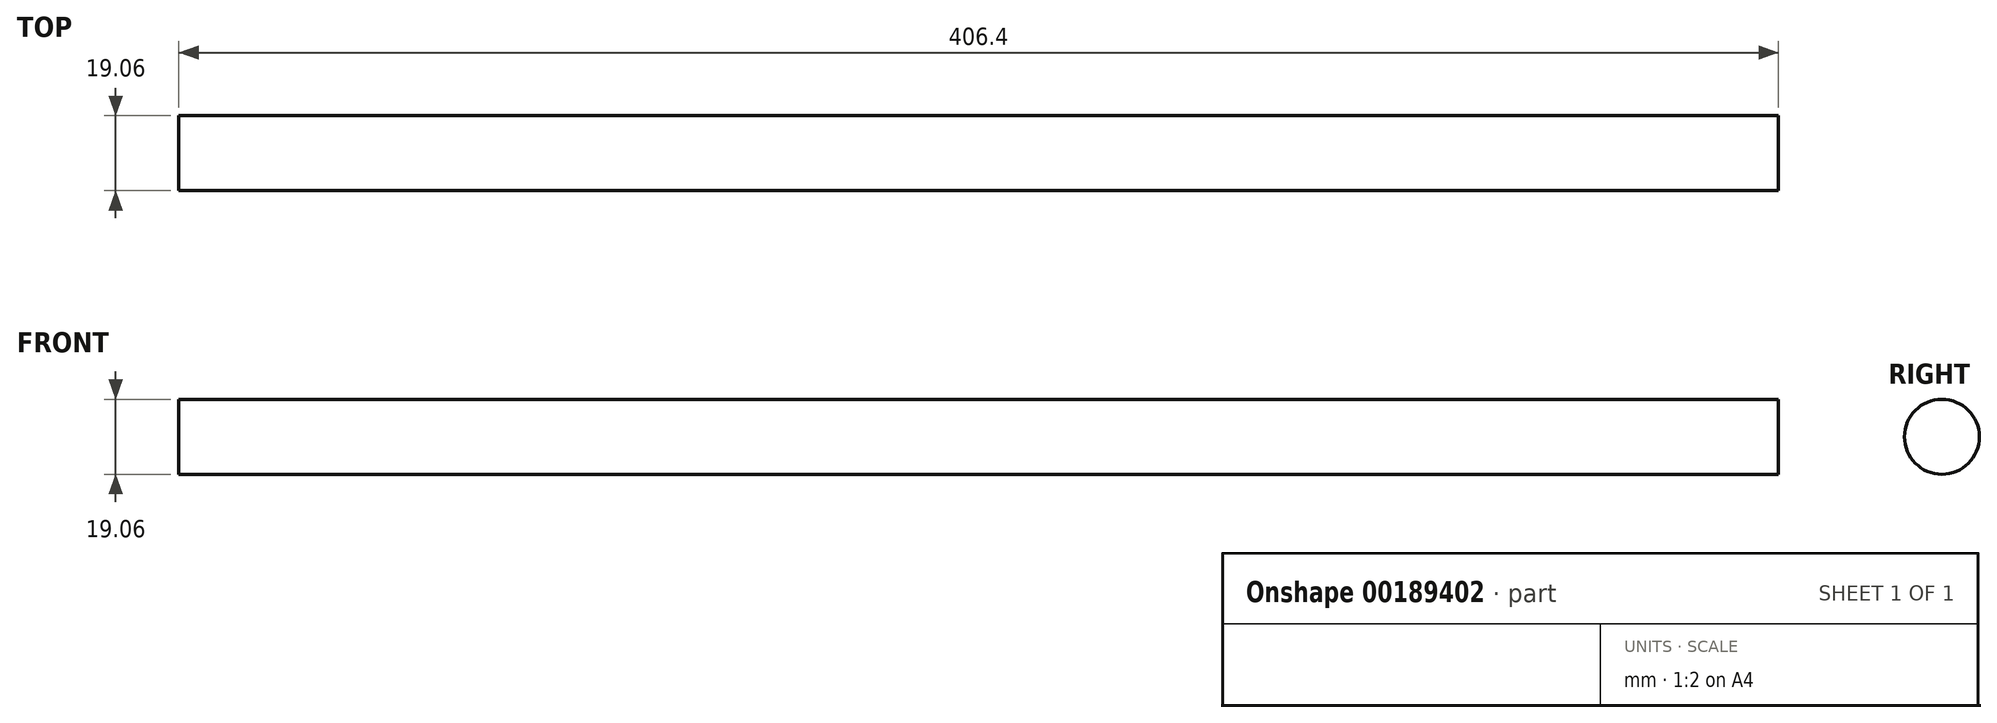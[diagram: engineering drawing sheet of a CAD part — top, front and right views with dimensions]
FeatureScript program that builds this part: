
annotation { "Feature Type Name" : "Feature", "Feature Type Description" : "" }
export const myFeature = defineFeature(function(context is Context, id is Id, definition is map)
    precondition{}
    {
        {
            var Q0;
            Q0=qCreatedBy(makeId("Right.planeOp"),FACE);
            var sketch = newSketch(context, id + "F0", { "sketchPlane" : qUnion([Q0])});
            skCircle(sketch, "E0", {"center": v(0, 0) * mm, "radius": 9.53 * mm});
            skSolve(sketch);
        }
        {
            var Q0;
            Q0 = qSketchRegion(id + "F0", true);
            extrude(context, id + "F1", {"entities" : qUnion([Q0]), "depth" : 203.2 * mm, "hasSecondDirection" : true, "secondDirectionOppositeDirection" : true, "secondDirectionDepth" : 203.2 * mm});
        }
    });
